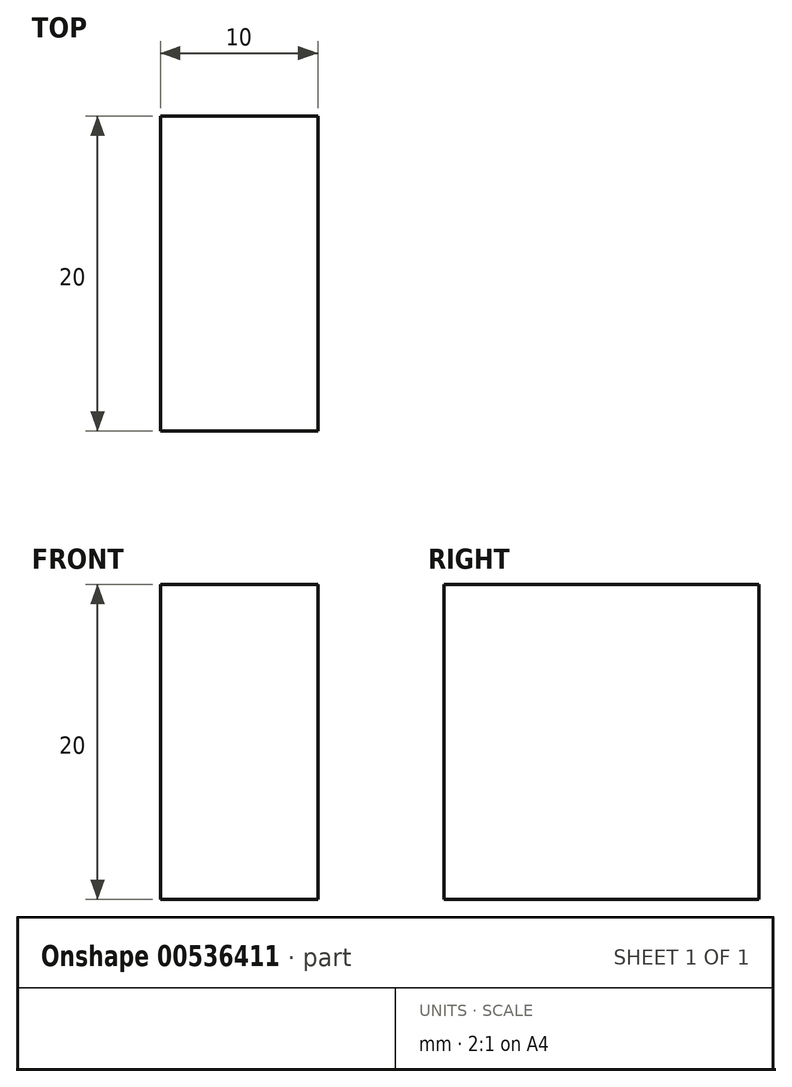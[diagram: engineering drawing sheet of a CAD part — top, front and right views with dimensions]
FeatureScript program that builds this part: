
annotation { "Feature Type Name" : "Feature", "Feature Type Description" : "" }
export const myFeature = defineFeature(function(context is Context, id is Id, definition is map)
    precondition{}
    {
        {
            var Q0;
            Q0=qCreatedBy(makeId("Front.planeOp"),FACE);
            var sketch = newSketch(context, id + "F0", { "sketchPlane" : qUnion([Q0])});
            skLineSegment(sketch, "E0.bottom", {"start": v(5, -10) * mm, "end": v(-5, -10) * mm});
            skLineSegment(sketch, "E0.top", {"start": v(5, 10) * mm, "end": v(-5, 10) * mm});
            skLineSegment(sketch, "E0.left", {"start": v(5, -10) * mm, "end": v(5, 10) * mm});
            skLineSegment(sketch, "E0.right", {"start": v(-5, -10) * mm, "end": v(-5, 10) * mm});
            skPoint(sketch, "E0.middle", {"position": v(0, 0) * mm});
            skSolve(sketch);
        }
        {
            var Q0;
            Q0=makeQuery(id+"F0.imprint","IMPRINT",FACE,{"disambiguationData":[TD([[makeQuery(id+"F0.imprint","IMPRINT",EDGE,{"derivedFrom":sQuery(id+"F0.wireOp",EDGE,"E0.bottom")}),-1.0]])]});
            extrude(context, id + "F1", {"entities" : qUnion([Q0]), "depth" : 20 * mm});
        }
    });
